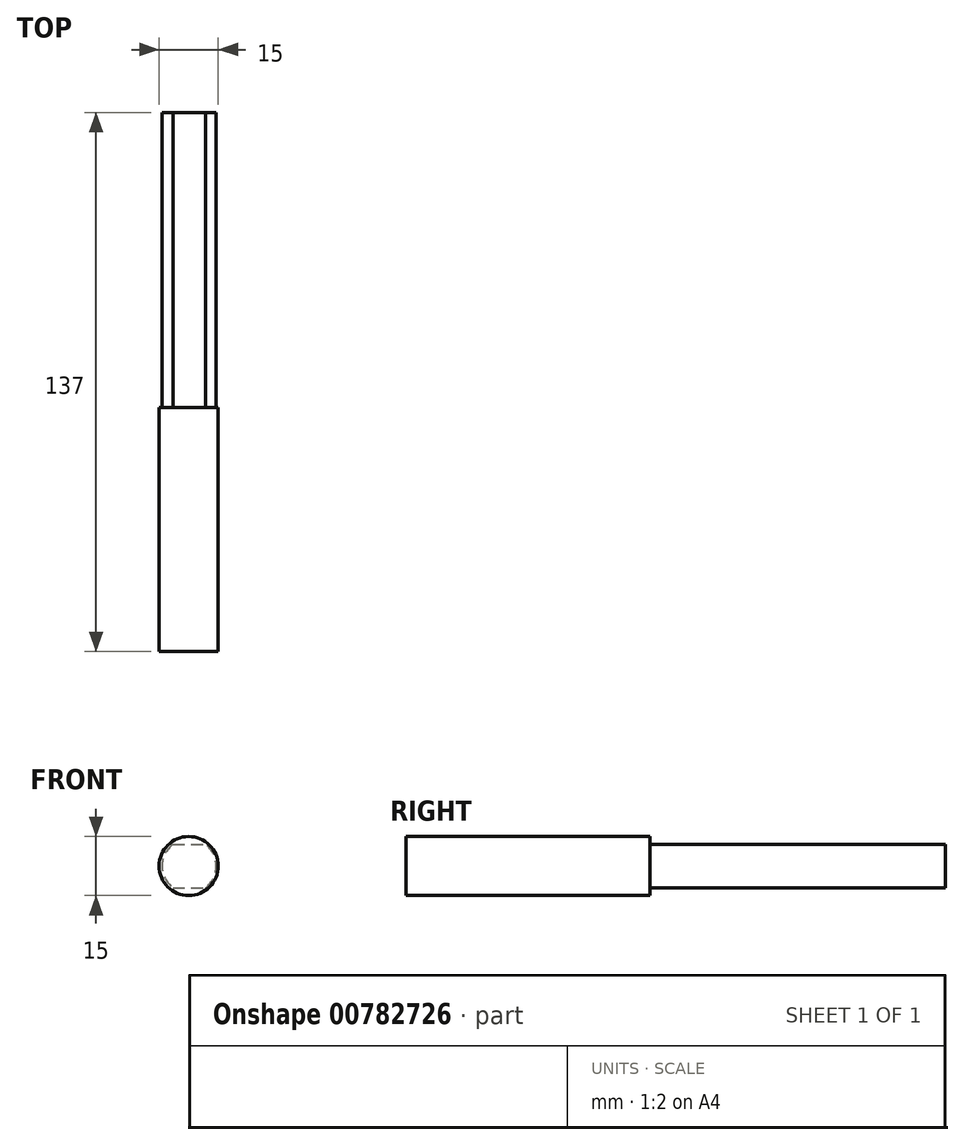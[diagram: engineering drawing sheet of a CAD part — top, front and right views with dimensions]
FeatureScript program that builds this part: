
annotation { "Feature Type Name" : "Feature", "Feature Type Description" : "" }
export const myFeature = defineFeature(function(context is Context, id is Id, definition is map)
    precondition{}
    {
        {
            var Q0;
            Q0=qCreatedBy(makeId("Front.planeOp"),FACE);
            var sketch = newSketch(context, id + "F0", { "sketchPlane" : qUnion([Q0])});
            skCircle(sketch, "E0", {"center": v(0, 0) * mm, "radius": 4 * mm});
            skLineSegment(sketch, "E1", {"start": v(-4.07, 5.5) * mm, "end": v(4.22, 5.5) * mm});
            skLineSegment(sketch, "E2", {"start": v(-4.07, -5.5) * mm, "end": v(4.22, -5.5) * mm});
            skArc(sketch, "E3", {"start": v(4.22, -5.5) * mm, "mid": v(6.9, 0) * mm, "end": v(4.22, 5.5) * mm});
            skArc(sketch, "E4", {"start": v(-4.07, 5.5) * mm, "mid": v(-6.84, 0) * mm, "end": v(-4.07, -5.5) * mm});
            skCircle(sketch, "E5", {"center": v(-0.09, 0) * mm, "radius": 7.5 * mm});
            skSolve(sketch);
        }
        {
            var Q0;
            Q0=makeQuery(id+"F0.imprint","IMPRINT",FACE,{"disambiguationData":[TD([[makeQuery(id+"F0.imprint","IMPRINT",EDGE,{"derivedFrom":sQuery(id+"F0.wireOp",EDGE,"E0")}),-1.0]])]});
            var Q1;
            Q1=makeQuery(id+"F0.imprint","IMPRINT",FACE,{"disambiguationData":[TD([[makeQuery(id+"F0.imprint","IMPRINT",EDGE,{"derivedFrom":sQuery(id+"F0.wireOp",EDGE,"E0")}),1.0]])]});
            extrude(context, id + "F1", {"entities" : qUnion([Q0, Q1]), "depth" : 130 * mm, "offsetDistance" : 25 * mm});
        }
        {
            var Q0;
            Q0 = qSketchRegion(id + "F0", true);
            extrude(context, id + "F2", {"entities" : qUnion([Q0]), "operationType" : NewBodyOperationType.ADD, "depth" : 137 * mm, "offsetDistance" : 25 * mm, "hasSecondDirection" : true, "secondDirectionOppositeDirection" : false, "secondDirectionDepth" : 75 * mm});
        }
        {
            var Q0;
            Q0=makeQuery(id+"F1.opExtrude","CAP_FACE",FACE,{"disambiguationData":[OSD([sQuery(id+"F0.wireOp",EDGE,"E1"),sQuery(id+"F0.wireOp",EDGE,"E2"),sQuery(id+"F0.wireOp",EDGE,"E3"),sQuery(id+"F0.wireOp",EDGE,"E4")])],"isStart":false});
            extrude(context, id + "F3", {"entities" : qUnion([Q0]), "operationType" : NewBodyOperationType.ADD, "depth" : 7 * mm, "offsetDistance" : 25 * mm});
        }
    });
